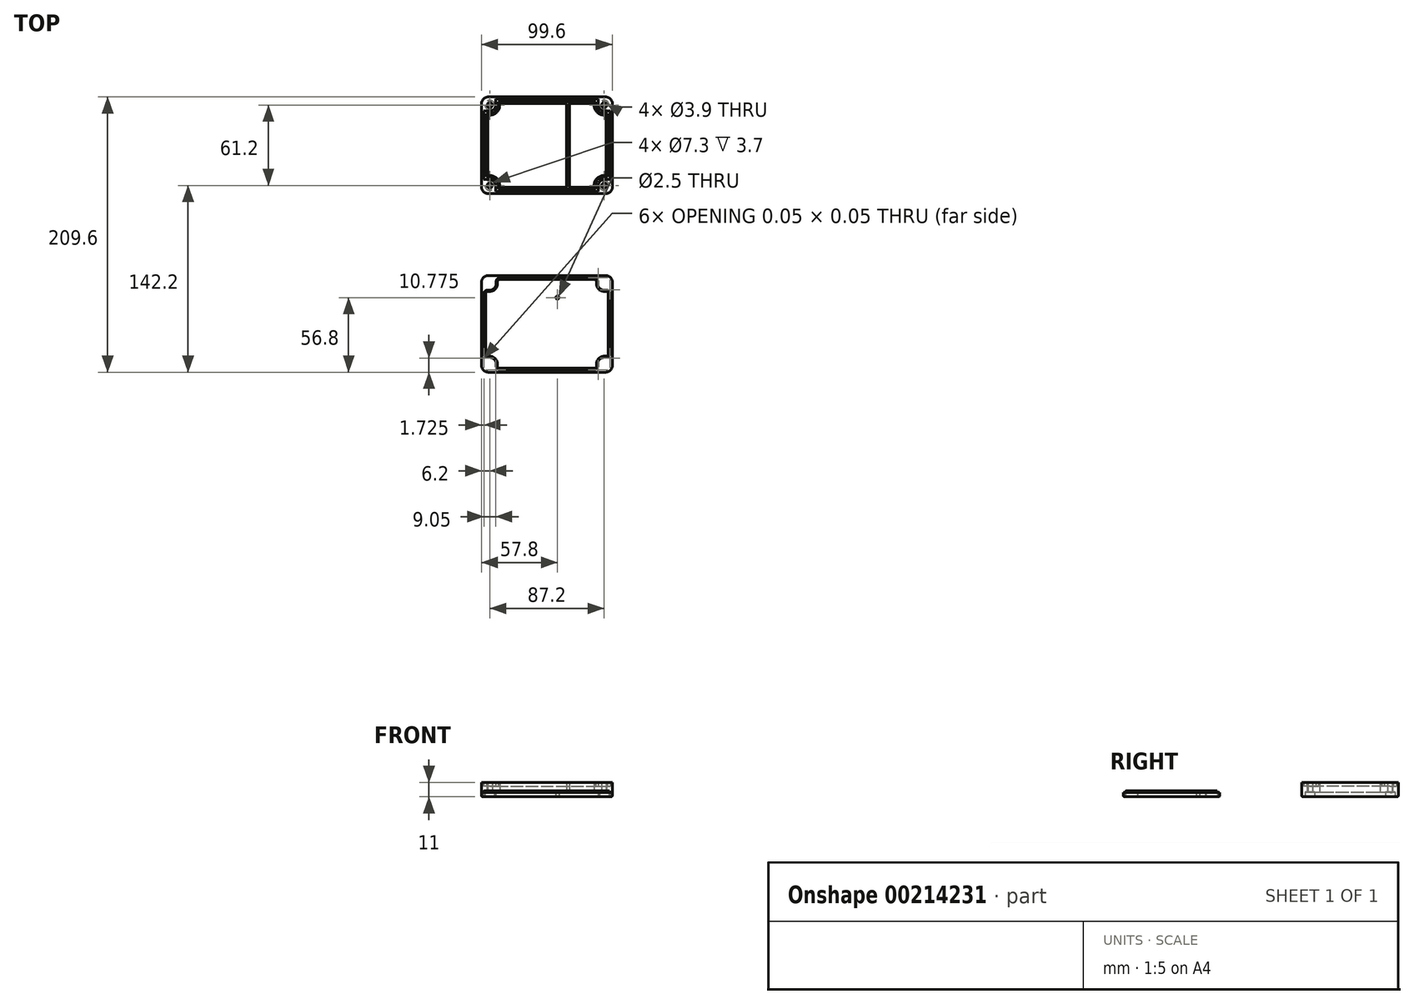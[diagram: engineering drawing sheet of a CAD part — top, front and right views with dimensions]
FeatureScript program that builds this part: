
annotation { "Feature Type Name" : "Feature", "Feature Type Description" : "" }
export const myFeature = defineFeature(function(context is Context, id is Id, definition is map)
    precondition{}
    {
        {
            var Q0;
            Q0=qCreatedBy(makeId("Top.planeOp"),FACE);
            var sketch = newSketch(context, id + "F0", { "sketchPlane" : qUnion([Q0])});
            skLineSegment(sketch, "E0.bottom", {"start": v(-25, 25) * mm, "end": v(25, 25) * mm, "construction": true});
            skLineSegment(sketch, "E0.top", {"start": v(-25, -25) * mm, "end": v(25, -25) * mm, "construction": true});
            skLineSegment(sketch, "E0.left", {"start": v(-25, 25) * mm, "end": v(-25, -25) * mm, "construction": true});
            skLineSegment(sketch, "E0.right", {"start": v(25, 25) * mm, "end": v(25, -25) * mm, "construction": true});
            skPoint(sketch, "E0.middle", {"position": v(0, 0) * mm});
            skLineSegment(sketch, "E1", {"start": v(-24, 32) * mm, "end": v(27, 32) * mm});
            skLineSegment(sketch, "E2", {"start": v(-33, 23) * mm, "end": v(-33, -23) * mm});
            skLineSegment(sketch, "E3", {"start": v(-24, -32) * mm, "end": v(27, -32) * mm});
            skLineSegment(sketch, "E4", {"start": v(28, 61.53) * mm, "end": v(28, -64.08) * mm, "construction": true});
            skLineSegment(sketch, "E5.bottom", {"start": v(31, 30) * mm, "end": v(47, 30) * mm, "construction": true});
            skLineSegment(sketch, "E5.top", {"start": v(31, -30) * mm, "end": v(47, -30) * mm, "construction": true});
            skLineSegment(sketch, "E5.left", {"start": v(31, 30) * mm, "end": v(31, -30) * mm, "construction": true});
            skLineSegment(sketch, "E5.right", {"start": v(47, 30) * mm, "end": v(47, -30) * mm, "construction": true});
            skPoint(sketch, "E5.middle", {"position": v(39, 0) * mm});
            skLineSegment(sketch, "E6", {"start": v(57, 23) * mm, "end": v(57, -23) * mm});
            skLineSegment(sketch, "E7", {"start": v(-32.8, 36.8) * mm, "end": v(56.8, 36.8) * mm});
            skLineSegment(sketch, "E8", {"start": v(-37.8, 31.8) * mm, "end": v(-37.8, -31.8) * mm});
            skLineSegment(sketch, "E9", {"start": v(-32.8, -36.8) * mm, "end": v(56.8, -36.8) * mm});
            skLineSegment(sketch, "E10", {"start": v(61.8, -31.8) * mm, "end": v(61.8, 31.8) * mm});
            skCircle(sketch, "E11", {"center": v(-31.6, 30.6) * mm, "radius": 1.95 * mm});
            skLineSegment(sketch, "E12.bottom", {"start": v(-25.1, 33.1) * mm, "end": v(49.1, 33.1) * mm});
            skLineSegment(sketch, "E12.top", {"start": v(-25.1, -33.1) * mm, "end": v(49.1, -33.1) * mm});
            skLineSegment(sketch, "E12.left", {"start": v(-34.1, 24.1) * mm, "end": v(-34.1, -24.1) * mm});
            skLineSegment(sketch, "E12.right", {"start": v(58.1, 24.1) * mm, "end": v(58.1, -24.1) * mm});
            skLineSegment(sketch, "E13.top", {"start": v(-27.1, -35.2) * mm, "end": v(51.1, -35.2) * mm});
            skLineSegment(sketch, "E13.right", {"start": v(60.2, 26.1) * mm, "end": v(60.2, -26.1) * mm});
            skLineSegment(sketch, "E14.trimOffspring", {"start": v(-27.1, 35.2) * mm, "end": v(51.1, 35.2) * mm});
            skLineSegment(sketch, "E15.trimOffspring", {"start": v(-36.2, 26.1) * mm, "end": v(-36.2, -26.1) * mm});
            skPoint(sketch, "E16.visualSharp", {"position": v(-37.8, 36.8) * mm});
            skArc(sketch, "E16.filletArc", {"start": v(-32.8, 36.8) * mm, "mid": v(-36.34, 35.34) * mm, "end": v(-37.8, 31.8) * mm});
            skLineSegment(sketch, "E17", {"start": v(27, 32) * mm, "end": v(27, -32) * mm});
            skLineSegment(sketch, "E18.MirrorCS", {"start": v(29, 32) * mm, "end": v(29, -32) * mm});
            skLineSegment(sketch, "E19.trimOffspring", {"start": v(29, 32) * mm, "end": v(48, 32) * mm});
            skLineSegment(sketch, "E20.trimOffspring", {"start": v(29, -32) * mm, "end": v(48, -32) * mm});
            skCircle(sketch, "E21", {"center": v(55.6, 30.6) * mm, "radius": 1.95 * mm});
            skArc(sketch, "E22", {"start": v(51.1, 30.6) * mm, "mid": v(52.42, 27.42) * mm, "end": v(55.6, 26.1) * mm});
            skArc(sketch, "E23", {"start": v(49.1, 30.6) * mm, "mid": v(51, 26) * mm, "end": v(55.6, 24.1) * mm});
            skArc(sketch, "E24", {"start": v(48, 30.6) * mm, "mid": v(50.23, 25.23) * mm, "end": v(55.6, 23) * mm});
            skCircle(sketch, "E25", {"center": v(55.6, -30.6) * mm, "radius": 1.95 * mm});
            skArc(sketch, "E26", {"start": v(55.6, -26.1) * mm, "mid": v(52.42, -27.42) * mm, "end": v(51.1, -30.6) * mm});
            skArc(sketch, "E27", {"start": v(55.6, -24.1) * mm, "mid": v(51, -26) * mm, "end": v(49.1, -30.6) * mm});
            skArc(sketch, "E28", {"start": v(55.6, -23) * mm, "mid": v(50.23, -25.23) * mm, "end": v(48, -30.6) * mm});
            skCircle(sketch, "E29", {"center": v(-31.6, -30.6) * mm, "radius": 1.95 * mm});
            skArc(sketch, "E30", {"start": v(-27.1, -30.6) * mm, "mid": v(-28.42, -27.42) * mm, "end": v(-31.6, -26.1) * mm});
            skArc(sketch, "E31", {"start": v(-25.1, -30.6) * mm, "mid": v(-27, -26) * mm, "end": v(-31.6, -24.1) * mm});
            skArc(sketch, "E32", {"start": v(-24, -30.6) * mm, "mid": v(-26.23, -25.23) * mm, "end": v(-31.6, -23) * mm});
            skLineSegment(sketch, "E33", {"start": v(48, 30.6) * mm, "end": v(48, 32) * mm});
            skLineSegment(sketch, "E34", {"start": v(49.1, 30.6) * mm, "end": v(49.1, 33.1) * mm});
            skLineSegment(sketch, "E35", {"start": v(51.1, 30.6) * mm, "end": v(51.1, 35.2) * mm});
            skLineSegment(sketch, "E36", {"start": v(55.6, 23) * mm, "end": v(57, 23) * mm});
            skLineSegment(sketch, "E37", {"start": v(55.6, 24.1) * mm, "end": v(58.1, 24.1) * mm});
            skLineSegment(sketch, "E38", {"start": v(55.6, 26.1) * mm, "end": v(60.2, 26.1) * mm});
            skLineSegment(sketch, "E39", {"start": v(55.6, -23) * mm, "end": v(57, -23) * mm});
            skLineSegment(sketch, "E40", {"start": v(55.6, -26.1) * mm, "end": v(60.2, -26.1) * mm});
            skLineSegment(sketch, "E41", {"start": v(48, -30.6) * mm, "end": v(48, -32) * mm});
            skLineSegment(sketch, "E42", {"start": v(49.1, -30.6) * mm, "end": v(49.1, -33.1) * mm});
            skLineSegment(sketch, "E43", {"start": v(51.1, -30.6) * mm, "end": v(51.1, -35.2) * mm});
            skLineSegment(sketch, "E44", {"start": v(55.6, -24.1) * mm, "end": v(58.1, -24.1) * mm});
            skArc(sketch, "E45", {"start": v(-31.6, 26.1) * mm, "mid": v(-28.42, 27.42) * mm, "end": v(-27.1, 30.6) * mm});
            skArc(sketch, "E46", {"start": v(-31.6, 24.1) * mm, "mid": v(-27, 26) * mm, "end": v(-25.1, 30.6) * mm});
            skArc(sketch, "E47", {"start": v(-31.6, 23) * mm, "mid": v(-26.23, 25.23) * mm, "end": v(-24, 30.6) * mm});
            skLineSegment(sketch, "E48", {"start": v(-24, 30.6) * mm, "end": v(-24, 32) * mm});
            skLineSegment(sketch, "E49", {"start": v(-25.1, 30.6) * mm, "end": v(-25.1, 33.1) * mm});
            skLineSegment(sketch, "E50", {"start": v(-27.1, 30.6) * mm, "end": v(-27.1, 35.2) * mm});
            skLineSegment(sketch, "E51", {"start": v(-31.6, 23) * mm, "end": v(-33, 23) * mm});
            skLineSegment(sketch, "E52", {"start": v(-31.6, 24.1) * mm, "end": v(-34.1, 24.1) * mm});
            skLineSegment(sketch, "E53", {"start": v(-31.6, 26.1) * mm, "end": v(-36.2, 26.1) * mm});
            skLineSegment(sketch, "E54", {"start": v(-24, -30.6) * mm, "end": v(-24, -32) * mm});
            skLineSegment(sketch, "E55", {"start": v(-25.1, -30.6) * mm, "end": v(-25.1, -33.1) * mm});
            skLineSegment(sketch, "E56", {"start": v(-27.1, -30.6) * mm, "end": v(-27.1, -35.2) * mm});
            skLineSegment(sketch, "E57", {"start": v(-31.6, -23) * mm, "end": v(-33, -23) * mm});
            skLineSegment(sketch, "E58", {"start": v(-31.6, -24.1) * mm, "end": v(-34.1, -24.1) * mm});
            skLineSegment(sketch, "E59", {"start": v(-31.6, -26.1) * mm, "end": v(-36.2, -26.1) * mm});
            skPoint(sketch, "E60.visualSharp", {"position": v(61.8, 36.8) * mm});
            skArc(sketch, "E60.filletArc", {"start": v(61.8, 31.8) * mm, "mid": v(60.34, 35.34) * mm, "end": v(56.8, 36.8) * mm});
            skPoint(sketch, "E61.visualSharp", {"position": v(61.8, -36.8) * mm});
            skArc(sketch, "E61.filletArc", {"start": v(56.8, -36.8) * mm, "mid": v(60.34, -35.34) * mm, "end": v(61.8, -31.8) * mm});
            skPoint(sketch, "E62.visualSharp", {"position": v(-37.8, -36.8) * mm});
            skArc(sketch, "E62.filletArc", {"start": v(-37.8, -31.8) * mm, "mid": v(-36.34, -35.34) * mm, "end": v(-32.8, -36.8) * mm});
            skSolve(sketch);
        }
        {
            var Q0;
            Q0=makeQuery(id+"F0.imprint","IMPRINT",FACE,{"disambiguationData":[TD([[makeQuery(id+"F0.imprint","IMPRINT",EDGE,{"derivedFrom":sQuery(id+"F0.wireOp",EDGE,"E7")}),-1.0]])]});
            var Q1;
            Q1=makeQuery(id+"F0.imprint","IMPRINT",FACE,{"disambiguationData":[TD([[makeQuery(id+"F0.imprint","IMPRINT",EDGE,{"derivedFrom":sQuery(id+"F0.wireOp",EDGE,"E1")}),1.0]])]});
            extrude(context, id + "F1", {"entities" : qUnion([Q0, Q1]), "depth" : 11 * mm});
        }
        {
            var Q0;
            Q0=makeQuery(id+"F0.imprint","IMPRINT",FACE,{"disambiguationData":[TD([[makeQuery(id+"F0.imprint","IMPRINT",EDGE,{"derivedFrom":sQuery(id+"F0.wireOp",EDGE,"E12.bottom")}),1.0]])]});
            extrude(context, id + "F2", {"entities" : qUnion([Q0]), "operationType" : NewBodyOperationType.ADD, "depth" : 8 * mm});
        }
        {
            var Q0;
            Q0=makeQuery(id+"F0.imprint","IMPRINT",FACE,{"disambiguationData":[TD([[makeQuery(id+"F0.imprint","IMPRINT",EDGE,{"derivedFrom":sQuery(id+"F0.wireOp",EDGE,"E6")}),-1.0]])]});
            var Q1;
            Q1=makeQuery(id+"F0.imprint","IMPRINT",FACE,{"disambiguationData":[TD([[makeQuery(id+"F0.imprint","IMPRINT",EDGE,{"derivedFrom":sQuery(id+"F0.wireOp",EDGE,"E1")}),-1.0]])]});
            extrude(context, id + "F3", {"entities" : qUnion([Q0, Q1]), "operationType" : NewBodyOperationType.ADD, "depth" : 3.2 * mm});
        }
        {
            var Q0;
            Q0=qCreatedBy(makeId("Top.planeOp"),FACE);
            var sketch = newSketch(context, id + "F4", { "sketchPlane" : qUnion([Q0])});
            skLineSegment(sketch, "E63", {"start": v(0, 0) * mm, "end": v(0, -187.5) * mm, "construction": true});
            skLineSegment(sketch, "E64", {"start": v(0, -136) * mm, "end": v(-72.43, -136) * mm, "construction": true});
            skLineSegment(sketch, "E65", {"start": v(0, -136) * mm, "end": v(90.36, -136) * mm, "construction": true});
            skLineSegment(sketch, "E66.bottom", {"start": v(-25, -111) * mm, "end": v(25, -111) * mm, "construction": true});
            skLineSegment(sketch, "E66.top", {"start": v(-25, -161) * mm, "end": v(25, -161) * mm, "construction": true});
            skLineSegment(sketch, "E66.left", {"start": v(-25, -111) * mm, "end": v(-25, -161) * mm, "construction": true});
            skLineSegment(sketch, "E66.right", {"start": v(25, -111) * mm, "end": v(25, -161) * mm, "construction": true});
            skPoint(sketch, "E66.middle", {"position": v(0, -136) * mm});
            skLineSegment(sketch, "E67.bottom", {"start": v(31, -106) * mm, "end": v(47, -106) * mm, "construction": true});
            skLineSegment(sketch, "E67.top", {"start": v(31, -166) * mm, "end": v(47, -166) * mm, "construction": true});
            skLineSegment(sketch, "E67.left", {"start": v(31, -106) * mm, "end": v(31, -166) * mm, "construction": true});
            skLineSegment(sketch, "E67.right", {"start": v(47, -106) * mm, "end": v(47, -166) * mm, "construction": true});
            skPoint(sketch, "E67.middle", {"position": v(39, -136) * mm});
            skLineSegment(sketch, "E68", {"start": v(28, -80.22) * mm, "end": v(28, -200.99) * mm, "construction": true});
            skLineSegment(sketch, "E69", {"start": v(-25.2, -102.8) * mm, "end": v(49.2, -102.8) * mm});
            skLineSegment(sketch, "E70", {"start": v(58.2, -111.8) * mm, "end": v(58.2, -160.2) * mm});
            skLineSegment(sketch, "E71", {"start": v(49.2, -169.2) * mm, "end": v(-25.2, -169.2) * mm});
            skLineSegment(sketch, "E72", {"start": v(-34.2, -160.2) * mm, "end": v(-34.2, -111.8) * mm});
            skLineSegment(sketch, "E73", {"start": v(-32.8, -99.2) * mm, "end": v(56.8, -99.2) * mm});
            skLineSegment(sketch, "E74", {"start": v(61.8, -104.2) * mm, "end": v(61.8, -167.8) * mm});
            skLineSegment(sketch, "E75", {"start": v(56.8, -172.8) * mm, "end": v(-32.8, -172.8) * mm});
            skLineSegment(sketch, "E76", {"start": v(-37.8, -167.8) * mm, "end": v(-37.8, -104.2) * mm});
            skLineSegment(sketch, "E77", {"start": v(-27, -100.9) * mm, "end": v(51.05, -100.9) * mm});
            skLineSegment(sketch, "E78", {"start": v(60.1, -109.95) * mm, "end": v(60.1, -162.05) * mm});
            skLineSegment(sketch, "E79", {"start": v(51.05, -171.1) * mm, "end": v(-27.05, -171.1) * mm});
            skLineSegment(sketch, "E80", {"start": v(-36.1, -162.05) * mm, "end": v(-36.1, -110) * mm});
            skCircle(sketch, "E81", {"center": v(-31.6, -105.4) * mm, "radius": 1.25 * mm});
            skCircle(sketch, "E82", {"center": v(55.6, -105.4) * mm, "radius": 1.25 * mm});
            skCircle(sketch, "E83", {"center": v(55.6, -166.6) * mm, "radius": 1.25 * mm});
            skCircle(sketch, "E84", {"center": v(-31.6, -166.6) * mm, "radius": 1.25 * mm});
            skArc(sketch, "E85", {"start": v(-31.6, -110) * mm, "mid": v(-28.35, -108.65) * mm, "end": v(-27, -105.4) * mm});
            skArc(sketch, "E86", {"start": v(-31.6, -111.8) * mm, "mid": v(-27.07, -109.93) * mm, "end": v(-25.2, -105.4) * mm});
            skLineSegment(sketch, "E87", {"start": v(-25.2, -105.4) * mm, "end": v(-25.2, -102.8) * mm});
            skLineSegment(sketch, "E88", {"start": v(-31.6, -111.8) * mm, "end": v(-34.2, -111.8) * mm});
            skLineSegment(sketch, "E89", {"start": v(-31.6, -110) * mm, "end": v(-36.1, -110) * mm});
            skLineSegment(sketch, "E90", {"start": v(-27, -105.4) * mm, "end": v(-27, -100.9) * mm});
            skArc(sketch, "E91", {"start": v(51, -105.4) * mm, "mid": v(52.35, -108.65) * mm, "end": v(55.6, -110) * mm});
            skArc(sketch, "E92", {"start": v(49.2, -105.4) * mm, "mid": v(51.07, -109.93) * mm, "end": v(55.6, -111.8) * mm});
            skArc(sketch, "E93", {"start": v(-27, -166.6) * mm, "mid": v(-28.35, -163.35) * mm, "end": v(-31.6, -162) * mm});
            skArc(sketch, "E94", {"start": v(-36.05, -162) * mm, "mid": v(-36.07, -162.02) * mm, "end": v(-36.1, -162.05) * mm});
            skArc(sketch, "E95", {"start": v(55.6, -162) * mm, "mid": v(52.35, -163.35) * mm, "end": v(51, -166.6) * mm});
            skArc(sketch, "E96", {"start": v(51, -171.05) * mm, "mid": v(51.02, -171.07) * mm, "end": v(51.05, -171.1) * mm});
            skLineSegment(sketch, "E97", {"start": v(49.2, -105.4) * mm, "end": v(49.2, -102.8) * mm});
            skLineSegment(sketch, "E98", {"start": v(51, -105.4) * mm, "end": v(51, -100.9) * mm});
            skLineSegment(sketch, "E99", {"start": v(55.6, -111.8) * mm, "end": v(58.2, -111.8) * mm});
            skLineSegment(sketch, "E100", {"start": v(55.6, -110) * mm, "end": v(60.1, -110) * mm});
            skLineSegment(sketch, "E101", {"start": v(55.6, -160.2) * mm, "end": v(58.2, -160.2) * mm});
            skLineSegment(sketch, "E102", {"start": v(55.6, -162) * mm, "end": v(60.1, -162) * mm});
            skLineSegment(sketch, "E103", {"start": v(49.2, -166.6) * mm, "end": v(49.2, -169.2) * mm});
            skLineSegment(sketch, "E104", {"start": v(51, -166.6) * mm, "end": v(51, -171.1) * mm});
            skLineSegment(sketch, "E105", {"start": v(-31.6, -160.2) * mm, "end": v(-34.2, -160.2) * mm});
            skLineSegment(sketch, "E106", {"start": v(-36.1, -162) * mm, "end": v(-31.6, -162) * mm});
            skLineSegment(sketch, "E107", {"start": v(-25.2, -166.6) * mm, "end": v(-25.2, -169.2) * mm});
            skLineSegment(sketch, "E108", {"start": v(-27, -166.6) * mm, "end": v(-27, -171.1) * mm});
            skArc(sketch, "E109.trimOffspring", {"start": v(51.05, -100.9) * mm, "mid": v(51.02, -100.93) * mm, "end": v(51, -100.95) * mm});
            skArc(sketch, "E110.trimOffspring", {"start": v(60.05, -110) * mm, "mid": v(60.07, -109.98) * mm, "end": v(60.1, -109.95) * mm});
            skArc(sketch, "E111.trimOffspring", {"start": v(60.1, -162.05) * mm, "mid": v(60.07, -162.02) * mm, "end": v(60.05, -162) * mm});
            skArc(sketch, "E112.trimOffspring", {"start": v(55.6, -160.2) * mm, "mid": v(51.07, -162.07) * mm, "end": v(49.2, -166.6) * mm});
            skArc(sketch, "E113.trimOffspring", {"start": v(-27.05, -171.1) * mm, "mid": v(-27.02, -171.07) * mm, "end": v(-27, -171.05) * mm});
            skArc(sketch, "E114.trimOffspring", {"start": v(-25.2, -166.6) * mm, "mid": v(-27.07, -162.07) * mm, "end": v(-31.6, -160.2) * mm});
            skCircle(sketch, "E115", {"center": v(-20, -116) * mm, "radius": 1.25 * mm});
            skCircle(sketch, "E116", {"center": v(-20, -116) * mm, "radius": 2.75 * mm});
            skCircle(sketch, "E117.MirrorC", {"center": v(20, -116) * mm, "radius": 2.75 * mm});
            skCircle(sketch, "E118.MirrorC", {"center": v(20, -116) * mm, "radius": 1.25 * mm});
            skCircle(sketch, "E119.MirrorC", {"center": v(-20, -156) * mm, "radius": 1.25 * mm});
            skCircle(sketch, "E120.MirrorC", {"center": v(-20, -156) * mm, "radius": 2.75 * mm});
            skCircle(sketch, "E121.MirrorC", {"center": v(20, -156) * mm, "radius": 1.25 * mm});
            skCircle(sketch, "E122.MirrorC", {"center": v(20, -156) * mm, "radius": 2.75 * mm});
            skPoint(sketch, "E123.visualSharp", {"position": v(-37.8, -99.2) * mm});
            skArc(sketch, "E123.filletArc", {"start": v(-32.8, -99.2) * mm, "mid": v(-36.34, -100.66) * mm, "end": v(-37.8, -104.2) * mm});
            skPoint(sketch, "E124.visualSharp", {"position": v(61.8, -99.2) * mm});
            skArc(sketch, "E124.filletArc", {"start": v(61.8, -104.2) * mm, "mid": v(60.34, -100.66) * mm, "end": v(56.8, -99.2) * mm});
            skPoint(sketch, "E125.visualSharp", {"position": v(61.8, -172.8) * mm});
            skArc(sketch, "E125.filletArc", {"start": v(56.8, -172.8) * mm, "mid": v(60.34, -171.34) * mm, "end": v(61.8, -167.8) * mm});
            skPoint(sketch, "E126.visualSharp", {"position": v(-37.8, -172.8) * mm});
            skArc(sketch, "E126.filletArc", {"start": v(-37.8, -167.8) * mm, "mid": v(-36.34, -171.34) * mm, "end": v(-32.8, -172.8) * mm});
            skLineSegment(sketch, "E127", {"start": v(27, -102.8) * mm, "end": v(27, -169.2) * mm});
            skLineSegment(sketch, "E128", {"start": v(29, -102.8) * mm, "end": v(29, -169.2) * mm});
            skSolve(sketch);
        }
        {
            var Q0;
            Q0=makeQuery(id+"F4.imprint","IMPRINT",FACE,{"disambiguationData":[TD([[makeQuery(id+"F4.imprint","IMPRINT",EDGE,{"derivedFrom":sQuery(id+"F4.wireOp",EDGE,"E73")}),-1.0]])]});
            var Q1;
            {var subQ0=sQuery(id+"F4.wireOp",EDGE,"E127");Q1=makeQuery(id+"F4.imprint","IMPRINT",FACE,{"disambiguationData":[TD([[makeQuery(id+"F4.imprint","IMPRINT",EDGE,{"derivedFrom":subQ0}),1.0]])]});}
            extrude(context, id + "F5", {"entities" : qUnion([Q0, Q1]), "depth" : 3.2 * mm});
        }
        {
            var Q0;
            Q0=makeQuery(id+"F4.imprint","IMPRINT",FACE,{"disambiguationData":[TD([[makeQuery(id+"F4.imprint","IMPRINT",EDGE,{"derivedFrom":sQuery(id+"F4.wireOp",EDGE,"E70")}),1.0]])]});
            extrude(context, id + "F6", {"entities" : qUnion([Q0]), "operationType" : NewBodyOperationType.ADD, "depth" : 4.7 * mm});
        }
        {
            var Q0;
            Q0=makeQuery(id+"F4.imprint","IMPRINT",FACE,{"disambiguationData":[TD([[makeQuery(id+"F4.imprint","IMPRINT",EDGE,{"derivedFrom":sQuery(id+"F4.wireOp",EDGE,"E81")}),1.0]])]});
            var Q1;
            Q1=makeQuery(id+"F4.imprint","IMPRINT",FACE,{"disambiguationData":[TD([[makeQuery(id+"F4.imprint","IMPRINT",EDGE,{"derivedFrom":sQuery(id+"F4.wireOp",EDGE,"E82")}),1.0]])]});
            var Q2;
            Q2=makeQuery(id+"F4.imprint","IMPRINT",FACE,{"disambiguationData":[TD([[makeQuery(id+"F4.imprint","IMPRINT",EDGE,{"derivedFrom":sQuery(id+"F4.wireOp",EDGE,"E84")}),1.0]])]});
            var Q3;
            Q3=makeQuery(id+"F4.imprint","IMPRINT",FACE,{"disambiguationData":[TD([[makeQuery(id+"F4.imprint","IMPRINT",EDGE,{"derivedFrom":sQuery(id+"F4.wireOp",EDGE,"E83")}),1.0]])]});
            var Q4;
            Q4=makeQuery(id+"F4.imprint","IMPRINT",FACE,{"disambiguationData":[TD([[makeQuery(id+"F4.imprint","IMPRINT",EDGE,{"derivedFrom":sQuery(id+"F4.wireOp",EDGE,"E70")}),-1.0]])]});
            var Q5;
            Q5=makeQuery(id+"F4.imprint","IMPRINT",FACE,{"disambiguationData":[TD([[makeQuery(id+"F4.imprint","IMPRINT",EDGE,{"derivedFrom":sQuery(id+"F4.wireOp",EDGE,"E72")}),-1.0]])]});
            extrude(context, id + "F7", {"entities" : qUnion([Q0, Q1, Q2, Q3, Q4, Q5]), "operationType" : NewBodyOperationType.ADD, "depth" : 3.2 * mm});
        }
        {
            var Q0;
            Q0=makeQuery(id+"F4.imprint","IMPRINT",FACE,{"disambiguationData":[TD([[makeQuery(id+"F4.imprint","IMPRINT",EDGE,{"derivedFrom":sQuery(id+"F4.wireOp",EDGE,"E115")}),-1.0]])]});
            var Q1;
            Q1=makeQuery(id+"F4.imprint","IMPRINT",FACE,{"disambiguationData":[TD([[makeQuery(id+"F4.imprint","IMPRINT",EDGE,{"derivedFrom":sQuery(id+"F4.wireOp",EDGE,"E119.MirrorC")}),1.0]])]});
            var Q2;
            Q2=makeQuery(id+"F4.imprint","IMPRINT",FACE,{"disambiguationData":[TD([[makeQuery(id+"F4.imprint","IMPRINT",EDGE,{"derivedFrom":sQuery(id+"F4.wireOp",EDGE,"E121.MirrorC")}),-1.0]])]});
            var Q3;
            Q3=makeQuery(id+"F4.imprint","IMPRINT",FACE,{"disambiguationData":[TD([[makeQuery(id+"F4.imprint","IMPRINT",EDGE,{"derivedFrom":sQuery(id+"F4.wireOp",EDGE,"E117.MirrorC")}),-1.0]])]});
            var Q4;
            {var subQ0=sQuery(id+"F4.wireOp",EDGE,"E128");var subQ1=sQuery(id+"F4.wireOp",EDGE,"E71");var subQ2=sQuery(id+"F4.wireOp",EDGE,"E69");var subQ3=sQuery(id+"F4.wireOp",EDGE,"E127");Q4=makeQuery(id+"F7.boolean.opBoolean","MERGE",FACE,{"derivedFrom":[makeQuery(id+"F5.opExtrude","CAP_FACE",FACE,{"disambiguationData":[OSD([subQ2,subQ1,subQ3,subQ0])],"isStart":false}),makeQuery(id+"F7.opExtrude","CAP_FACE",FACE,{"disambiguationData":[OSD([subQ2,subQ1,sQuery(id+"F4.wireOp",EDGE,"E72"),sQuery(id+"F4.wireOp",EDGE,"E86"),sQuery(id+"F4.wireOp",EDGE,"E87"),sQuery(id+"F4.wireOp",EDGE,"E88"),sQuery(id+"F4.wireOp",EDGE,"E105"),sQuery(id+"F4.wireOp",EDGE,"E107"),sQuery(id+"F4.wireOp",EDGE,"E114.trimOffspring"),sQuery(id+"F4.wireOp",EDGE,"E116"),sQuery(id+"F4.wireOp",EDGE,"E117.MirrorC"),sQuery(id+"F4.wireOp",EDGE,"E120.MirrorC"),sQuery(id+"F4.wireOp",EDGE,"E122.MirrorC"),subQ3])],"isStart":false}),makeQuery(id+"F7.opExtrude","CAP_FACE",FACE,{"disambiguationData":[OSD([subQ2,sQuery(id+"F4.wireOp",EDGE,"E70"),subQ1,sQuery(id+"F4.wireOp",EDGE,"E92"),sQuery(id+"F4.wireOp",EDGE,"E97"),sQuery(id+"F4.wireOp",EDGE,"E99"),sQuery(id+"F4.wireOp",EDGE,"E101"),sQuery(id+"F4.wireOp",EDGE,"E103"),sQuery(id+"F4.wireOp",EDGE,"E112.trimOffspring"),subQ0])],"isStart":false})]});}
            extrude(context, id + "F8", {"entities" : qUnion([Q0, Q1, Q2, Q3]), "operationType" : NewBodyOperationType.ADD, "endBound" : BoundingType.UP_TO_SURFACE, "endBoundEntityFace" : qUnion([Q4]), "depth" : 13.2 * mm});
        }
        {
            var Q0;
            Q0=makeQuery(id+"F4.imprint","IMPRINT",FACE,{"disambiguationData":[TD([[makeQuery(id+"F4.imprint","IMPRINT",EDGE,{"derivedFrom":sQuery(id+"F4.wireOp",EDGE,"E115")}),1.0]])]});
            var Q1;
            Q1=makeQuery(id+"F4.imprint","IMPRINT",FACE,{"disambiguationData":[TD([[makeQuery(id+"F4.imprint","IMPRINT",EDGE,{"derivedFrom":sQuery(id+"F4.wireOp",EDGE,"E118.MirrorC")}),-1.0]])]});
            var Q2;
            Q2=makeQuery(id+"F4.imprint","IMPRINT",FACE,{"disambiguationData":[TD([[makeQuery(id+"F4.imprint","IMPRINT",EDGE,{"derivedFrom":sQuery(id+"F4.wireOp",EDGE,"E121.MirrorC")}),1.0]])]});
            var Q3;
            Q3=makeQuery(id+"F4.imprint","IMPRINT",FACE,{"disambiguationData":[TD([[makeQuery(id+"F4.imprint","IMPRINT",EDGE,{"derivedFrom":sQuery(id+"F4.wireOp",EDGE,"E119.MirrorC")}),-1.0]])]});
            var Q4;
            Q4=makeQuery(id+"F7.opExtrude","CAP_FACE",FACE,{"disambiguationData":[OSD([sQuery(id+"F4.wireOp",EDGE,"E69"),sQuery(id+"F4.wireOp",EDGE,"E71"),sQuery(id+"F4.wireOp",EDGE,"E72"),sQuery(id+"F4.wireOp",EDGE,"E86"),sQuery(id+"F4.wireOp",EDGE,"E87"),sQuery(id+"F4.wireOp",EDGE,"E88"),sQuery(id+"F4.wireOp",EDGE,"E105"),sQuery(id+"F4.wireOp",EDGE,"E107"),sQuery(id+"F4.wireOp",EDGE,"E114.trimOffspring"),sQuery(id+"F4.wireOp",EDGE,"E116"),sQuery(id+"F4.wireOp",EDGE,"E117.MirrorC"),sQuery(id+"F4.wireOp",EDGE,"E120.MirrorC"),sQuery(id+"F4.wireOp",EDGE,"E122.MirrorC"),sQuery(id+"F4.wireOp",EDGE,"E127")])],"isStart":false});
            extrude(context, id + "F9", {"entities" : qUnion([Q0, Q1, Q2, Q3]), "operationType" : NewBodyOperationType.ADD, "endBound" : BoundingType.UP_TO_SURFACE, "endBoundEntityFace" : qUnion([Q4]), "depth" : 25 * mm});
        }
        {
            var Q0;
            Q0=makeQuery(id+"F5.opExtrude","SWEPT_EDGE",EDGE,{"disambiguationData":[OSD([sQuery(id+"F4.wireOp",EDGE,"E69"),sQuery(id+"F4.wireOp",EDGE,"E127")])]});
            var Q1;
            Q1=makeQuery(id+"F6.opExtrude","SWEPT_EDGE",EDGE,{"disambiguationData":[OSD([sQuery(id+"F4.wireOp",EDGE,"E69"),sQuery(id+"F4.wireOp",EDGE,"E97")])]});
            var Q2;
            Q2=makeQuery(id+"F6.opExtrude","SWEPT_EDGE",EDGE,{"disambiguationData":[OSD([sQuery(id+"F4.wireOp",EDGE,"E70"),sQuery(id+"F4.wireOp",EDGE,"E99")])]});
            var Q3;
            Q3=makeQuery(id+"F6.opExtrude","SWEPT_EDGE",EDGE,{"disambiguationData":[OSD([sQuery(id+"F4.wireOp",EDGE,"E70"),sQuery(id+"F4.wireOp",EDGE,"E101")])]});
            var Q4;
            Q4=makeQuery(id+"F6.opExtrude","SWEPT_EDGE",EDGE,{"disambiguationData":[OSD([sQuery(id+"F4.wireOp",EDGE,"E71"),sQuery(id+"F4.wireOp",EDGE,"E103")])]});
            var Q5;
            Q5=makeQuery(id+"F5.opExtrude","SWEPT_EDGE",EDGE,{"disambiguationData":[OSD([sQuery(id+"F4.wireOp",EDGE,"E71"),sQuery(id+"F4.wireOp",EDGE,"E128")])]});
            var Q6;
            Q6=makeQuery(id+"F5.opExtrude","SWEPT_EDGE",EDGE,{"disambiguationData":[OSD([sQuery(id+"F4.wireOp",EDGE,"E69"),sQuery(id+"F4.wireOp",EDGE,"E128")])]});
            var Q7;
            Q7=makeQuery(id+"F5.opExtrude","SWEPT_EDGE",EDGE,{"disambiguationData":[OSD([sQuery(id+"F4.wireOp",EDGE,"E71"),sQuery(id+"F4.wireOp",EDGE,"E127")])]});
            var Q8;
            Q8=makeQuery(id+"F6.opExtrude","SWEPT_EDGE",EDGE,{"disambiguationData":[OSD([sQuery(id+"F4.wireOp",EDGE,"E69"),sQuery(id+"F4.wireOp",EDGE,"E87")])]});
            var Q9;
            Q9=makeQuery(id+"F6.opExtrude","SWEPT_EDGE",EDGE,{"disambiguationData":[OSD([sQuery(id+"F4.wireOp",EDGE,"E72"),sQuery(id+"F4.wireOp",EDGE,"E88")])]});
            var Q10;
            Q10=makeQuery(id+"F6.opExtrude","SWEPT_EDGE",EDGE,{"disambiguationData":[OSD([sQuery(id+"F4.wireOp",EDGE,"E71"),sQuery(id+"F4.wireOp",EDGE,"E107")])]});
            var Q11;
            Q11=makeQuery(id+"F6.opExtrude","SWEPT_EDGE",EDGE,{"disambiguationData":[OSD([sQuery(id+"F4.wireOp",EDGE,"E72"),sQuery(id+"F4.wireOp",EDGE,"E105")])]});
            fillet(context, id + "F10", {"entities" : qUnion([Q0, Q1, Q2, Q3, Q4, Q5, Q6, Q7, Q8, Q9, Q10, Q11]), "radius" : 1 * mm, "tangentPropagation" : true, "allowEdgeOverflow" : false});
        }
        {
            var Q0;
            Q0=makeQuery(id+"F1.opExtrude","SWEPT_EDGE",EDGE,{"disambiguationData":[OSD([sQuery(id+"F0.wireOp",EDGE,"E2"),sQuery(id+"F0.wireOp",EDGE,"E57")])]});
            var Q1;
            Q1=makeQuery(id+"F1.opExtrude","SWEPT_EDGE",EDGE,{"disambiguationData":[OSD([sQuery(id+"F0.wireOp",EDGE,"E3"),sQuery(id+"F0.wireOp",EDGE,"E54")])]});
            var Q2;
            Q2=makeQuery(id+"F1.opExtrude","SWEPT_EDGE",EDGE,{"disambiguationData":[OSD([sQuery(id+"F0.wireOp",EDGE,"E2"),sQuery(id+"F0.wireOp",EDGE,"E51")])]});
            var Q3;
            Q3=makeQuery(id+"F1.opExtrude","SWEPT_EDGE",EDGE,{"disambiguationData":[OSD([sQuery(id+"F0.wireOp",EDGE,"E1"),sQuery(id+"F0.wireOp",EDGE,"E48")])]});
            var Q4;
            Q4=makeQuery(id+"F1.opExtrude","SWEPT_EDGE",EDGE,{"disambiguationData":[OSD([sQuery(id+"F0.wireOp",EDGE,"E3"),sQuery(id+"F0.wireOp",EDGE,"E17")])]});
            var Q5;
            Q5=makeQuery(id+"F1.opExtrude","SWEPT_EDGE",EDGE,{"disambiguationData":[OSD([sQuery(id+"F0.wireOp",EDGE,"E1"),sQuery(id+"F0.wireOp",EDGE,"E17")])]});
            var Q6;
            Q6=makeQuery(id+"F1.opExtrude","SWEPT_EDGE",EDGE,{"disambiguationData":[OSD([sQuery(id+"F0.wireOp",EDGE,"E20.trimOffspring"),sQuery(id+"F0.wireOp",EDGE,"E41")])]});
            var Q7;
            Q7=makeQuery(id+"F1.opExtrude","SWEPT_EDGE",EDGE,{"disambiguationData":[OSD([sQuery(id+"F0.wireOp",EDGE,"E6"),sQuery(id+"F0.wireOp",EDGE,"E39")])]});
            var Q8;
            Q8=makeQuery(id+"F1.opExtrude","SWEPT_EDGE",EDGE,{"disambiguationData":[OSD([sQuery(id+"F0.wireOp",EDGE,"E18.MirrorCS"),sQuery(id+"F0.wireOp",EDGE,"E20.trimOffspring")])]});
            var Q9;
            Q9=makeQuery(id+"F1.opExtrude","SWEPT_EDGE",EDGE,{"disambiguationData":[OSD([sQuery(id+"F0.wireOp",EDGE,"E6"),sQuery(id+"F0.wireOp",EDGE,"E36")])]});
            var Q10;
            Q10=makeQuery(id+"F1.opExtrude","SWEPT_EDGE",EDGE,{"disambiguationData":[OSD([sQuery(id+"F0.wireOp",EDGE,"E19.trimOffspring"),sQuery(id+"F0.wireOp",EDGE,"E33")])]});
            var Q11;
            Q11=makeQuery(id+"F1.opExtrude","SWEPT_EDGE",EDGE,{"disambiguationData":[OSD([sQuery(id+"F0.wireOp",EDGE,"E18.MirrorCS"),sQuery(id+"F0.wireOp",EDGE,"E19.trimOffspring")])]});
            fillet(context, id + "F11", {"entities" : qUnion([Q0, Q1, Q2, Q3, Q4, Q5, Q6, Q7, Q8, Q9, Q10, Q11]), "radius" : 1 * mm, "tangentPropagation" : true, "allowEdgeOverflow" : false});
        }
        {
            var Q0;
            {var subQ0=sQuery(id+"F0.wireOp",EDGE,"E41");var subQ1=sQuery(id+"F0.wireOp",EDGE,"E39");var subQ2=sQuery(id+"F0.wireOp",EDGE,"E36");var subQ3=sQuery(id+"F0.wireOp",EDGE,"E33");var subQ4=sQuery(id+"F0.wireOp",EDGE,"E28");var subQ5=sQuery(id+"F0.wireOp",EDGE,"E24");var subQ6=sQuery(id+"F0.wireOp",EDGE,"E20.trimOffspring");var subQ7=sQuery(id+"F0.wireOp",EDGE,"E19.trimOffspring");var subQ8=sQuery(id+"F0.wireOp",EDGE,"E18.MirrorCS");var subQ9=sQuery(id+"F0.wireOp",EDGE,"E6");var subQ10=sQuery(id+"F0.wireOp",EDGE,"E57");var subQ11=sQuery(id+"F0.wireOp",EDGE,"E54");var subQ12=sQuery(id+"F0.wireOp",EDGE,"E51");var subQ13=sQuery(id+"F0.wireOp",EDGE,"E48");var subQ14=sQuery(id+"F0.wireOp",EDGE,"E47");var subQ15=sQuery(id+"F0.wireOp",EDGE,"E32");var subQ16=sQuery(id+"F0.wireOp",EDGE,"E17");var subQ17=sQuery(id+"F0.wireOp",EDGE,"E3");var subQ18=sQuery(id+"F0.wireOp",EDGE,"E2");var subQ19=sQuery(id+"F0.wireOp",EDGE,"E1");var subQ20=sQuery(id+"F0.wireOp",EDGE,"E59");var subQ21=sQuery(id+"F0.wireOp",EDGE,"E58");var subQ22=sQuery(id+"F0.wireOp",EDGE,"E56");var subQ23=sQuery(id+"F0.wireOp",EDGE,"E55");var subQ24=sQuery(id+"F0.wireOp",EDGE,"E53");var subQ25=sQuery(id+"F0.wireOp",EDGE,"E52");var subQ26=sQuery(id+"F0.wireOp",EDGE,"E50");var subQ27=sQuery(id+"F0.wireOp",EDGE,"E49");var subQ28=sQuery(id+"F0.wireOp",EDGE,"E46");var subQ29=sQuery(id+"F0.wireOp",EDGE,"E45");var subQ30=sQuery(id+"F0.wireOp",EDGE,"E44");var subQ31=sQuery(id+"F0.wireOp",EDGE,"E43");var subQ32=sQuery(id+"F0.wireOp",EDGE,"E42");var subQ33=sQuery(id+"F0.wireOp",EDGE,"E40");var subQ34=sQuery(id+"F0.wireOp",EDGE,"E38");var subQ35=sQuery(id+"F0.wireOp",EDGE,"E37");var subQ36=sQuery(id+"F0.wireOp",EDGE,"E35");var subQ37=sQuery(id+"F0.wireOp",EDGE,"E34");var subQ38=sQuery(id+"F0.wireOp",EDGE,"E31");var subQ39=sQuery(id+"F0.wireOp",EDGE,"E30");var subQ40=sQuery(id+"F0.wireOp",EDGE,"E27");var subQ41=sQuery(id+"F0.wireOp",EDGE,"E26");var subQ42=sQuery(id+"F0.wireOp",EDGE,"E23");var subQ43=sQuery(id+"F0.wireOp",EDGE,"E22");var subQ44=sQuery(id+"F0.wireOp",EDGE,"E15.trimOffspring");var subQ45=sQuery(id+"F0.wireOp",EDGE,"E14.trimOffspring");var subQ46=sQuery(id+"F0.wireOp",EDGE,"E13.right");var subQ47=sQuery(id+"F0.wireOp",EDGE,"E13.top");var subQ48=sQuery(id+"F0.wireOp",EDGE,"E12.right");var subQ49=sQuery(id+"F0.wireOp",EDGE,"E12.left");var subQ50=sQuery(id+"F0.wireOp",EDGE,"E12.top");var subQ51=sQuery(id+"F0.wireOp",EDGE,"E12.bottom");Q0=makeQuery(id+"F3.boolean.opBoolean","MERGE",FACE,{"derivedFrom":[makeQuery(id+"F2.boolean.opBoolean","MERGE",FACE,{"derivedFrom":[makeQuery(id+"F1.opExtrude","CAP_FACE",FACE,{"disambiguationData":[OSD([subQ19,subQ18,subQ17,subQ9,subQ51,subQ50,subQ49,subQ48,subQ16,subQ8,subQ7,subQ6,subQ42,subQ5,subQ40,subQ4,subQ38,subQ15,subQ3,subQ37,subQ2,subQ35,subQ1,subQ0,subQ32,subQ30,subQ28,subQ14,subQ13,subQ27,subQ12,subQ25,subQ11,subQ23,subQ10,subQ21])],"isStart":true}),makeQuery(id+"F1.opExtrude","CAP_FACE",FACE,{"disambiguationData":[OSD([sQuery(id+"F0.wireOp",EDGE,"E7"),sQuery(id+"F0.wireOp",EDGE,"E8"),sQuery(id+"F0.wireOp",EDGE,"E9"),sQuery(id+"F0.wireOp",EDGE,"E10"),sQuery(id+"F0.wireOp",EDGE,"E11"),subQ47,subQ46,subQ45,subQ44,sQuery(id+"F0.wireOp",EDGE,"E16.filletArc"),sQuery(id+"F0.wireOp",EDGE,"E21"),subQ43,sQuery(id+"F0.wireOp",EDGE,"E25"),subQ41,sQuery(id+"F0.wireOp",EDGE,"E29"),subQ39,subQ36,subQ34,subQ33,subQ31,subQ29,subQ26,subQ24,subQ22,subQ20,sQuery(id+"F0.wireOp",EDGE,"E60.filletArc"),sQuery(id+"F0.wireOp",EDGE,"E61.filletArc"),sQuery(id+"F0.wireOp",EDGE,"E62.filletArc")])],"isStart":true}),makeQuery(id+"F2.opExtrude","CAP_FACE",FACE,{"disambiguationData":[OSD([subQ51,subQ50,subQ49,subQ48,subQ47,subQ46,subQ45,subQ44,subQ43,subQ42,subQ41,subQ40,subQ39,subQ38,subQ37,subQ36,subQ35,subQ34,subQ33,subQ32,subQ31,subQ30,subQ29,subQ28,subQ27,subQ26,subQ25,subQ24,subQ23,subQ22,subQ21,subQ20])],"isStart":true})]}),makeQuery(id+"F3.opExtrude","CAP_FACE",FACE,{"disambiguationData":[OSD([subQ19,subQ18,subQ17,subQ16,subQ15,subQ14,subQ13,subQ12,subQ11,subQ10])],"isStart":true}),makeQuery(id+"F3.opExtrude","CAP_FACE",FACE,{"disambiguationData":[OSD([subQ9,subQ8,subQ7,subQ6,subQ5,subQ4,subQ3,subQ2,subQ1,subQ0])],"isStart":true})]});}
            var sketch = newSketch(context, id + "F12", { "sketchPlane" : qUnion([Q0])});
            skCircle(sketch, "E129", {"center": v(55.6, -30.6) * mm, "radius": 3.65 * mm});
            skCircle(sketch, "E130", {"center": v(-31.6, -30.6) * mm, "radius": 3.65 * mm});
            skCircle(sketch, "E131", {"center": v(-31.6, 30.6) * mm, "radius": 3.65 * mm});
            skCircle(sketch, "E132", {"center": v(55.6, 30.6) * mm, "radius": 3.65 * mm});
            skSolve(sketch);
        }
        {
            var Q0;
            Q0=makeQuery(id+"F12.imprint","IMPRINT",FACE,{"disambiguationData":[TD([[makeQuery(id+"F12.imprint","IMPRINT",EDGE,{"derivedFrom":sQuery(id+"F12.wireOp",EDGE,"E129")}),1.0]])]});
            var Q1;
            Q1=makeQuery(id+"F12.imprint","IMPRINT",FACE,{"disambiguationData":[TD([[makeQuery(id+"F12.imprint","IMPRINT",EDGE,{"derivedFrom":sQuery(id+"F12.wireOp",EDGE,"E132")}),1.0]])]});
            var Q2;
            Q2=makeQuery(id+"F12.imprint","IMPRINT",FACE,{"disambiguationData":[TD([[makeQuery(id+"F12.imprint","IMPRINT",EDGE,{"derivedFrom":sQuery(id+"F12.wireOp",EDGE,"E130")}),1.0]])]});
            var Q3;
            Q3=makeQuery(id+"F12.imprint","IMPRINT",FACE,{"disambiguationData":[TD([[makeQuery(id+"F12.imprint","IMPRINT",EDGE,{"derivedFrom":sQuery(id+"F12.wireOp",EDGE,"E131")}),1.0]])]});
            extrude(context, id + "F13", {"entities" : qUnion([Q0, Q1, Q2, Q3]), "operationType" : NewBodyOperationType.REMOVE, "oppositeDirection" : true, "depth" : 3.7 * mm});
        }
        {
            var Q0;
            Q0=makeQuery(id+"F5.opExtrude","CAP_EDGE",EDGE,{"disambiguationData":[OSD([sQuery(id+"F4.wireOp",EDGE,"E74")])],"isStart":true});
            var Q1;
            Q1=makeQuery(id+"F5.opExtrude","CAP_EDGE",EDGE,{"disambiguationData":[OSD([sQuery(id+"F4.wireOp",EDGE,"E125.filletArc")])],"isStart":true});
            var Q2;
            Q2=makeQuery(id+"F5.opExtrude","CAP_EDGE",EDGE,{"disambiguationData":[OSD([sQuery(id+"F4.wireOp",EDGE,"E75")])],"isStart":true});
            var Q3;
            Q3=makeQuery(id+"F5.opExtrude","CAP_EDGE",EDGE,{"disambiguationData":[OSD([sQuery(id+"F4.wireOp",EDGE,"E126.filletArc")])],"isStart":true});
            var Q4;
            Q4=makeQuery(id+"F5.opExtrude","CAP_EDGE",EDGE,{"disambiguationData":[OSD([sQuery(id+"F4.wireOp",EDGE,"E76")])],"isStart":true});
            var Q5;
            Q5=makeQuery(id+"F5.opExtrude","CAP_EDGE",EDGE,{"disambiguationData":[OSD([sQuery(id+"F4.wireOp",EDGE,"E123.filletArc")])],"isStart":true});
            var Q6;
            Q6=makeQuery(id+"F5.opExtrude","CAP_EDGE",EDGE,{"disambiguationData":[OSD([sQuery(id+"F4.wireOp",EDGE,"E73")])],"isStart":true});
            var Q7;
            Q7=makeQuery(id+"F5.opExtrude","CAP_EDGE",EDGE,{"disambiguationData":[OSD([sQuery(id+"F4.wireOp",EDGE,"E124.filletArc")])],"isStart":true});
            fillet(context, id + "F14", {"entities" : qUnion([Q0, Q1, Q2, Q3, Q4, Q5, Q6, Q7]), "radius" : 1 * mm, "tangentPropagation" : true, "allowEdgeOverflow" : false});
        }
        {
            var Q0;
            Q0=makeQuery(id+"F1.opExtrude","CAP_EDGE",EDGE,{"disambiguationData":[OSD([sQuery(id+"F0.wireOp",EDGE,"E61.filletArc")])],"isStart":true});
            fillet(context, id + "F15", {"entities" : qUnion([Q0]), "radius" : 1 * mm, "tangentPropagation" : true, "allowEdgeOverflow" : false});
        }
        {
            var Q0;
            Q0=makeQuery(id+"F6.opExtrude","CAP_FACE",FACE,{"disambiguationData":[OSD([sQuery(id+"F4.wireOp",EDGE,"E69"),sQuery(id+"F4.wireOp",EDGE,"E70"),sQuery(id+"F4.wireOp",EDGE,"E71"),sQuery(id+"F4.wireOp",EDGE,"E72"),sQuery(id+"F4.wireOp",EDGE,"E77"),sQuery(id+"F4.wireOp",EDGE,"E78"),sQuery(id+"F4.wireOp",EDGE,"E79"),sQuery(id+"F4.wireOp",EDGE,"E80"),sQuery(id+"F4.wireOp",EDGE,"E85"),sQuery(id+"F4.wireOp",EDGE,"E86"),sQuery(id+"F4.wireOp",EDGE,"E87"),sQuery(id+"F4.wireOp",EDGE,"E88"),sQuery(id+"F4.wireOp",EDGE,"E89"),sQuery(id+"F4.wireOp",EDGE,"E90"),sQuery(id+"F4.wireOp",EDGE,"E91"),sQuery(id+"F4.wireOp",EDGE,"E92"),sQuery(id+"F4.wireOp",EDGE,"E93"),sQuery(id+"F4.wireOp",EDGE,"E95"),sQuery(id+"F4.wireOp",EDGE,"E97"),sQuery(id+"F4.wireOp",EDGE,"E98"),sQuery(id+"F4.wireOp",EDGE,"E99"),sQuery(id+"F4.wireOp",EDGE,"E100"),sQuery(id+"F4.wireOp",EDGE,"E101"),sQuery(id+"F4.wireOp",EDGE,"E102"),sQuery(id+"F4.wireOp",EDGE,"E103"),sQuery(id+"F4.wireOp",EDGE,"E104"),sQuery(id+"F4.wireOp",EDGE,"E105"),sQuery(id+"F4.wireOp",EDGE,"E106"),sQuery(id+"F4.wireOp",EDGE,"E107"),sQuery(id+"F4.wireOp",EDGE,"E108"),sQuery(id+"F4.wireOp",EDGE,"E112.trimOffspring"),sQuery(id+"F4.wireOp",EDGE,"E114.trimOffspring")])],"isStart":false});
            var sketch = newSketch(context, id + "F16", { "sketchPlane" : qUnion([Q0])});
            skLineSegment(sketch, "E133.0", {"start": v(-36.1, -162) * mm, "end": v(-36.1, -110) * mm});
            skLineSegment(sketch, "E133.1", {"start": v(-31.6, -110) * mm, "end": v(-36.1, -110) * mm});
            skArc(sketch, "E133.2", {"start": v(-31.6, -110) * mm, "mid": v(-28.35, -108.65) * mm, "end": v(-27, -105.4) * mm});
            skLineSegment(sketch, "E133.3", {"start": v(-27, -105.4) * mm, "end": v(-27, -100.9) * mm});
            skLineSegment(sketch, "E133.4", {"start": v(-27, -100.9) * mm, "end": v(51, -100.9) * mm});
            skLineSegment(sketch, "E133.5", {"start": v(51, -105.4) * mm, "end": v(51, -100.9) * mm});
            skArc(sketch, "E133.6", {"start": v(51, -105.4) * mm, "mid": v(52.35, -108.65) * mm, "end": v(55.6, -110) * mm});
            skLineSegment(sketch, "E133.7", {"start": v(55.6, -110) * mm, "end": v(60.1, -110) * mm});
            skLineSegment(sketch, "E133.8", {"start": v(60.1, -110) * mm, "end": v(60.1, -162) * mm});
            skLineSegment(sketch, "E133.9", {"start": v(55.6, -162) * mm, "end": v(60.1, -162) * mm});
            skArc(sketch, "E133.10", {"start": v(55.6, -162) * mm, "mid": v(52.35, -163.35) * mm, "end": v(51, -166.6) * mm});
            skLineSegment(sketch, "E133.11", {"start": v(51, -166.6) * mm, "end": v(51, -171.1) * mm});
            skLineSegment(sketch, "E133.12", {"start": v(51, -171.1) * mm, "end": v(-27, -171.1) * mm});
            skArc(sketch, "E133.13", {"start": v(-27, -166.6) * mm, "mid": v(-28.35, -163.35) * mm, "end": v(-31.6, -162) * mm});
            skLineSegment(sketch, "E133.14", {"start": v(-36.1, -162) * mm, "end": v(-31.6, -162) * mm});
            skLineSegment(sketch, "E133.15", {"start": v(-27, -166.6) * mm, "end": v(-27, -171.1) * mm});
            skLineSegment(sketch, "E134.0", {"start": v(-26.6, -105.4) * mm, "end": v(-26.6, -101.3) * mm});
            skArc(sketch, "E134.1", {"start": v(-31.6, -110.4) * mm, "mid": v(-28.06, -108.94) * mm, "end": v(-26.6, -105.4) * mm});
            skLineSegment(sketch, "E134.2", {"start": v(-31.6, -110.4) * mm, "end": v(-35.7, -110.4) * mm});
            skLineSegment(sketch, "E134.3", {"start": v(-35.7, -161.6) * mm, "end": v(-35.7, -110.4) * mm});
            skLineSegment(sketch, "E134.4", {"start": v(-35.7, -161.6) * mm, "end": v(-31.6, -161.6) * mm});
            skLineSegment(sketch, "E134.5", {"start": v(59.7, -110.4) * mm, "end": v(59.7, -161.6) * mm});
            skLineSegment(sketch, "E134.6", {"start": v(55.6, -110.4) * mm, "end": v(59.7, -110.4) * mm});
            skArc(sketch, "E134.7", {"start": v(50.6, -105.4) * mm, "mid": v(52.06, -108.94) * mm, "end": v(55.6, -110.4) * mm});
            skLineSegment(sketch, "E134.8", {"start": v(50.6, -105.4) * mm, "end": v(50.6, -101.3) * mm});
            skLineSegment(sketch, "E134.9", {"start": v(55.6, -161.6) * mm, "end": v(59.7, -161.6) * mm});
            skArc(sketch, "E134.10", {"start": v(55.6, -161.6) * mm, "mid": v(52.06, -163.06) * mm, "end": v(50.6, -166.6) * mm});
            skLineSegment(sketch, "E134.11", {"start": v(50.6, -166.6) * mm, "end": v(50.6, -170.7) * mm});
            skLineSegment(sketch, "E134.12", {"start": v(50.6, -170.7) * mm, "end": v(-26.6, -170.7) * mm});
            skLineSegment(sketch, "E134.13", {"start": v(-26.6, -166.6) * mm, "end": v(-26.6, -170.7) * mm});
            skLineSegment(sketch, "E134.14", {"start": v(-26.6, -101.3) * mm, "end": v(50.6, -101.3) * mm});
            skArc(sketch, "E134.15", {"start": v(-26.6, -166.6) * mm, "mid": v(-28.06, -163.06) * mm, "end": v(-31.6, -161.6) * mm});
            skLineSegment(sketch, "E135.0", {"start": v(-24.2, -102.8) * mm, "end": v(48.2, -102.8) * mm});
            skArc(sketch, "E135.1", {"start": v(-31.6, -111.8) * mm, "mid": v(-27.07, -109.93) * mm, "end": v(-25.2, -105.4) * mm});
            skLineSegment(sketch, "E135.2", {"start": v(-25.2, -105.4) * mm, "end": v(-25.2, -103.8) * mm});
            skArc(sketch, "E135.3", {"start": v(-25.2, -103.8) * mm, "mid": v(-24.9, -103.1) * mm, "end": v(-24.2, -102.8) * mm});
            skLineSegment(sketch, "E135.4", {"start": v(-31.6, -111.8) * mm, "end": v(-33.2, -111.8) * mm});
            skArc(sketch, "E135.5", {"start": v(-34.2, -112.8) * mm, "mid": v(-33.9, -112.1) * mm, "end": v(-33.2, -111.8) * mm});
            skLineSegment(sketch, "E135.6", {"start": v(-34.2, -159.2) * mm, "end": v(-34.2, -112.8) * mm});
            skArc(sketch, "E135.7", {"start": v(48.2, -102.8) * mm, "mid": v(48.9, -103.1) * mm, "end": v(49.2, -103.8) * mm});
            skLineSegment(sketch, "E135.8", {"start": v(49.2, -105.4) * mm, "end": v(49.2, -103.8) * mm});
            skArc(sketch, "E135.9", {"start": v(49.2, -105.4) * mm, "mid": v(51.07, -109.93) * mm, "end": v(55.6, -111.8) * mm});
            skLineSegment(sketch, "E135.10", {"start": v(55.6, -111.8) * mm, "end": v(57.2, -111.8) * mm});
            skArc(sketch, "E135.11", {"start": v(57.2, -111.8) * mm, "mid": v(57.9, -112.1) * mm, "end": v(58.2, -112.8) * mm});
            skArc(sketch, "E135.12", {"start": v(58.2, -159.2) * mm, "mid": v(57.9, -159.9) * mm, "end": v(57.2, -160.2) * mm});
            skLineSegment(sketch, "E135.13", {"start": v(55.6, -160.2) * mm, "end": v(57.2, -160.2) * mm});
            skArc(sketch, "E135.14", {"start": v(55.6, -160.2) * mm, "mid": v(51.07, -162.07) * mm, "end": v(49.2, -166.6) * mm});
            skArc(sketch, "E135.15", {"start": v(49.2, -168.2) * mm, "mid": v(48.9, -168.9) * mm, "end": v(48.2, -169.2) * mm});
            skLineSegment(sketch, "E135.16", {"start": v(49.2, -166.6) * mm, "end": v(49.2, -168.2) * mm});
            skArc(sketch, "E135.17", {"start": v(-33.2, -160.2) * mm, "mid": v(-33.9, -159.9) * mm, "end": v(-34.2, -159.2) * mm});
            skLineSegment(sketch, "E135.18", {"start": v(-31.6, -160.2) * mm, "end": v(-33.2, -160.2) * mm});
            skArc(sketch, "E135.19", {"start": v(-25.2, -166.6) * mm, "mid": v(-27.07, -162.07) * mm, "end": v(-31.6, -160.2) * mm});
            skLineSegment(sketch, "E135.20", {"start": v(-25.2, -166.6) * mm, "end": v(-25.2, -168.2) * mm});
            skArc(sketch, "E135.21", {"start": v(-24.2, -169.2) * mm, "mid": v(-24.9, -168.9) * mm, "end": v(-25.2, -168.2) * mm});
            skLineSegment(sketch, "E135.22", {"start": v(48.2, -169.2) * mm, "end": v(-24.2, -169.2) * mm});
            skLineSegment(sketch, "E135.23", {"start": v(58.2, -112.8) * mm, "end": v(58.2, -159.2) * mm});
            skArc(sketch, "E136.0", {"start": v(57.2, -111.3) * mm, "mid": v(58.26, -111.74) * mm, "end": v(58.7, -112.8) * mm});
            skLineSegment(sketch, "E136.1", {"start": v(-31.6, -160.7) * mm, "end": v(-33.2, -160.7) * mm});
            skArc(sketch, "E136.2", {"start": v(-25.7, -166.6) * mm, "mid": v(-27.43, -162.43) * mm, "end": v(-31.6, -160.7) * mm});
            skLineSegment(sketch, "E136.3", {"start": v(-25.7, -166.6) * mm, "end": v(-25.7, -168.2) * mm});
            skArc(sketch, "E136.4", {"start": v(-24.2, -169.7) * mm, "mid": v(-25.26, -169.26) * mm, "end": v(-25.7, -168.2) * mm});
            skLineSegment(sketch, "E136.5", {"start": v(48.2, -169.7) * mm, "end": v(-24.2, -169.7) * mm});
            skArc(sketch, "E136.6", {"start": v(49.7, -168.2) * mm, "mid": v(49.26, -169.26) * mm, "end": v(48.2, -169.7) * mm});
            skArc(sketch, "E136.7", {"start": v(58.7, -159.2) * mm, "mid": v(58.26, -160.26) * mm, "end": v(57.2, -160.7) * mm});
            skLineSegment(sketch, "E136.8", {"start": v(55.6, -160.7) * mm, "end": v(57.2, -160.7) * mm});
            skArc(sketch, "E136.9", {"start": v(55.6, -160.7) * mm, "mid": v(51.43, -162.43) * mm, "end": v(49.7, -166.6) * mm});
            skLineSegment(sketch, "E136.10", {"start": v(49.7, -166.6) * mm, "end": v(49.7, -168.2) * mm});
            skArc(sketch, "E136.11", {"start": v(-33.2, -160.7) * mm, "mid": v(-34.26, -160.26) * mm, "end": v(-34.7, -159.2) * mm});
            skLineSegment(sketch, "E136.12", {"start": v(58.7, -112.8) * mm, "end": v(58.7, -159.2) * mm});
            skLineSegment(sketch, "E136.13", {"start": v(-34.7, -159.2) * mm, "end": v(-34.7, -112.8) * mm});
            skArc(sketch, "E136.14", {"start": v(-34.7, -112.8) * mm, "mid": v(-34.26, -111.74) * mm, "end": v(-33.2, -111.3) * mm});
            skLineSegment(sketch, "E136.15", {"start": v(-31.6, -111.3) * mm, "end": v(-33.2, -111.3) * mm});
            skArc(sketch, "E136.16", {"start": v(-31.6, -111.3) * mm, "mid": v(-27.43, -109.57) * mm, "end": v(-25.7, -105.4) * mm});
            skLineSegment(sketch, "E136.17", {"start": v(-25.7, -105.4) * mm, "end": v(-25.7, -103.8) * mm});
            skArc(sketch, "E136.18", {"start": v(-25.7, -103.8) * mm, "mid": v(-25.26, -102.74) * mm, "end": v(-24.2, -102.3) * mm});
            skLineSegment(sketch, "E136.19", {"start": v(-24.2, -102.3) * mm, "end": v(48.2, -102.3) * mm});
            skArc(sketch, "E136.20", {"start": v(48.2, -102.3) * mm, "mid": v(49.26, -102.74) * mm, "end": v(49.7, -103.8) * mm});
            skLineSegment(sketch, "E136.21", {"start": v(49.7, -105.4) * mm, "end": v(49.7, -103.8) * mm});
            skArc(sketch, "E136.22", {"start": v(49.7, -105.4) * mm, "mid": v(51.43, -109.57) * mm, "end": v(55.6, -111.3) * mm});
            skLineSegment(sketch, "E136.23", {"start": v(55.6, -111.3) * mm, "end": v(57.2, -111.3) * mm});
            skSolve(sketch);
        }
        {
            var Q0;
            Q0=makeQuery(id+"F16.imprint","IMPRINT",FACE,{"disambiguationData":[TD([[makeQuery(id+"F16.imprint","IMPRINT",EDGE,{"derivedFrom":sQuery(id+"F16.wireOp",EDGE,"E133.0")}),-1.0]])]});
            var Q1;
            Q1=makeQuery(id+"F5.opExtrude","CAP_FACE",FACE,{"disambiguationData":[OSD([sQuery(id+"F4.wireOp",EDGE,"E73"),sQuery(id+"F4.wireOp",EDGE,"E74"),sQuery(id+"F4.wireOp",EDGE,"E75"),sQuery(id+"F4.wireOp",EDGE,"E76"),sQuery(id+"F4.wireOp",EDGE,"E77"),sQuery(id+"F4.wireOp",EDGE,"E78"),sQuery(id+"F4.wireOp",EDGE,"E79"),sQuery(id+"F4.wireOp",EDGE,"E80"),sQuery(id+"F4.wireOp",EDGE,"E81"),sQuery(id+"F4.wireOp",EDGE,"E82"),sQuery(id+"F4.wireOp",EDGE,"E83"),sQuery(id+"F4.wireOp",EDGE,"E84"),sQuery(id+"F4.wireOp",EDGE,"E85"),sQuery(id+"F4.wireOp",EDGE,"E89"),sQuery(id+"F4.wireOp",EDGE,"E90"),sQuery(id+"F4.wireOp",EDGE,"E91"),sQuery(id+"F4.wireOp",EDGE,"E93"),sQuery(id+"F4.wireOp",EDGE,"E94"),sQuery(id+"F4.wireOp",EDGE,"E95"),sQuery(id+"F4.wireOp",EDGE,"E96"),sQuery(id+"F4.wireOp",EDGE,"E98"),sQuery(id+"F4.wireOp",EDGE,"E100"),sQuery(id+"F4.wireOp",EDGE,"E102"),sQuery(id+"F4.wireOp",EDGE,"E104"),sQuery(id+"F4.wireOp",EDGE,"E106"),sQuery(id+"F4.wireOp",EDGE,"E108"),sQuery(id+"F4.wireOp",EDGE,"E109.trimOffspring"),sQuery(id+"F4.wireOp",EDGE,"E110.trimOffspring"),sQuery(id+"F4.wireOp",EDGE,"E111.trimOffspring"),sQuery(id+"F4.wireOp",EDGE,"E113.trimOffspring"),sQuery(id+"F4.wireOp",EDGE,"E123.filletArc"),sQuery(id+"F4.wireOp",EDGE,"E124.filletArc"),sQuery(id+"F4.wireOp",EDGE,"E125.filletArc"),sQuery(id+"F4.wireOp",EDGE,"E126.filletArc")])],"isStart":false});
            extrude(context, id + "F17", {"entities" : qUnion([Q0]), "operationType" : NewBodyOperationType.REMOVE, "endBound" : BoundingType.UP_TO_SURFACE, "oppositeDirection" : true, "endBoundEntityFace" : qUnion([Q1]), "depth" : 25 * mm});
        }
        {
            var Q0;
            Q0=makeQuery(id+"F16.imprint","IMPRINT",FACE,{"disambiguationData":[TD([[makeQuery(id+"F16.imprint","IMPRINT",EDGE,{"derivedFrom":sQuery(id+"F16.wireOp",EDGE,"E135.0")}),1.0]])]});
            var Q1;
            {var subQ0=sQuery(id+"F4.wireOp",EDGE,"E126.filletArc");var subQ1=sQuery(id+"F4.wireOp",EDGE,"E125.filletArc");var subQ2=sQuery(id+"F4.wireOp",EDGE,"E124.filletArc");var subQ3=sQuery(id+"F4.wireOp",EDGE,"E123.filletArc");var subQ4=sQuery(id+"F4.wireOp",EDGE,"E113.trimOffspring");var subQ5=sQuery(id+"F4.wireOp",EDGE,"E111.trimOffspring");var subQ6=sQuery(id+"F4.wireOp",EDGE,"E110.trimOffspring");var subQ7=sQuery(id+"F4.wireOp",EDGE,"E109.trimOffspring");var subQ8=sQuery(id+"F4.wireOp",EDGE,"E108");var subQ9=sQuery(id+"F4.wireOp",EDGE,"E106");var subQ10=sQuery(id+"F4.wireOp",EDGE,"E104");var subQ11=sQuery(id+"F4.wireOp",EDGE,"E102");var subQ12=sQuery(id+"F4.wireOp",EDGE,"E100");var subQ13=sQuery(id+"F4.wireOp",EDGE,"E98");var subQ14=sQuery(id+"F4.wireOp",EDGE,"E96");var subQ15=sQuery(id+"F4.wireOp",EDGE,"E95");var subQ16=sQuery(id+"F4.wireOp",EDGE,"E94");var subQ17=sQuery(id+"F4.wireOp",EDGE,"E93");var subQ18=sQuery(id+"F4.wireOp",EDGE,"E91");var subQ19=sQuery(id+"F4.wireOp",EDGE,"E90");var subQ20=sQuery(id+"F4.wireOp",EDGE,"E89");var subQ21=sQuery(id+"F4.wireOp",EDGE,"E85");var subQ22=sQuery(id+"F4.wireOp",EDGE,"E84");var subQ23=sQuery(id+"F4.wireOp",EDGE,"E83");var subQ24=sQuery(id+"F4.wireOp",EDGE,"E82");var subQ25=sQuery(id+"F4.wireOp",EDGE,"E81");var subQ26=sQuery(id+"F4.wireOp",EDGE,"E80");var subQ27=sQuery(id+"F4.wireOp",EDGE,"E79");var subQ28=sQuery(id+"F4.wireOp",EDGE,"E78");var subQ29=sQuery(id+"F4.wireOp",EDGE,"E77");var subQ30=sQuery(id+"F4.wireOp",EDGE,"E76");var subQ31=sQuery(id+"F4.wireOp",EDGE,"E75");var subQ32=sQuery(id+"F4.wireOp",EDGE,"E74");var subQ33=sQuery(id+"F4.wireOp",EDGE,"E73");Q1=makeQuery(id+"F17.boolean.opBoolean","MERGE",FACE,{"derivedFrom":[makeQuery(id+"F5.opExtrude","CAP_FACE",FACE,{"disambiguationData":[OSD([subQ33,subQ32,subQ31,subQ30,subQ29,subQ28,subQ27,subQ26,subQ25,subQ24,subQ23,subQ22,subQ21,subQ20,subQ19,subQ18,subQ17,subQ16,subQ15,subQ14,subQ13,subQ12,subQ11,subQ10,subQ9,subQ8,subQ7,subQ6,subQ5,subQ4,subQ3,subQ2,subQ1,subQ0])],"isStart":false}),makeQuery(id+"F17.opExtrude","CAP_FACE",FACE,{"disambiguationData":[OSD([subQ33,subQ32,subQ31,subQ30,subQ29,subQ28,subQ27,subQ26,subQ25,subQ24,subQ23,subQ22,subQ21,subQ20,subQ19,subQ18,subQ17,subQ16,subQ15,subQ14,subQ13,subQ12,subQ11,subQ10,subQ9,subQ8,subQ7,subQ6,subQ5,subQ4,subQ3,subQ2,subQ1,subQ0])],"isStart":false})]});}
            extrude(context, id + "F18", {"entities" : qUnion([Q0]), "operationType" : NewBodyOperationType.REMOVE, "endBound" : BoundingType.UP_TO_SURFACE, "oppositeDirection" : true, "endBoundEntityFace" : qUnion([Q1]), "depth" : 25 * mm});
        }
        {
            var Q0;
            Q0=makeQuery(id+"F17.boolean.opBoolean","COPY",EDGE,{"derivedFrom":makeQuery(id+"F17.opExtrude","SWEPT_EDGE",EDGE,{"disambiguationData":[OSD([sQuery(id+"F16.wireOp",EDGE,"E134.5"),sQuery(id+"F16.wireOp",EDGE,"E134.9")])]})});
            var Q1;
            Q1=makeQuery(id+"F17.boolean.opBoolean","COPY",EDGE,{"derivedFrom":makeQuery(id+"F17.opExtrude","SWEPT_EDGE",EDGE,{"disambiguationData":[OSD([sQuery(id+"F16.wireOp",EDGE,"E134.11"),sQuery(id+"F16.wireOp",EDGE,"E134.12")])]})});
            var Q2;
            Q2=makeQuery(id+"F17.boolean.opBoolean","COPY",EDGE,{"derivedFrom":makeQuery(id+"F17.opExtrude","SWEPT_EDGE",EDGE,{"disambiguationData":[OSD([sQuery(id+"F16.wireOp",EDGE,"E134.12"),sQuery(id+"F16.wireOp",EDGE,"E134.13")])]})});
            var Q3;
            Q3=makeQuery(id+"F17.boolean.opBoolean","COPY",EDGE,{"derivedFrom":makeQuery(id+"F17.opExtrude","SWEPT_EDGE",EDGE,{"disambiguationData":[OSD([sQuery(id+"F16.wireOp",EDGE,"E134.3"),sQuery(id+"F16.wireOp",EDGE,"E134.4")])]})});
            var Q4;
            Q4=makeQuery(id+"F17.boolean.opBoolean","COPY",EDGE,{"derivedFrom":makeQuery(id+"F17.opExtrude","SWEPT_EDGE",EDGE,{"disambiguationData":[OSD([sQuery(id+"F16.wireOp",EDGE,"E134.2"),sQuery(id+"F16.wireOp",EDGE,"E134.3")])]})});
            var Q5;
            Q5=makeQuery(id+"F17.boolean.opBoolean","COPY",EDGE,{"derivedFrom":makeQuery(id+"F17.opExtrude","SWEPT_EDGE",EDGE,{"disambiguationData":[OSD([sQuery(id+"F16.wireOp",EDGE,"E134.0"),sQuery(id+"F16.wireOp",EDGE,"E134.14")])]})});
            var Q6;
            Q6=makeQuery(id+"F17.boolean.opBoolean","COPY",EDGE,{"derivedFrom":makeQuery(id+"F17.opExtrude","SWEPT_EDGE",EDGE,{"disambiguationData":[OSD([sQuery(id+"F16.wireOp",EDGE,"E134.8"),sQuery(id+"F16.wireOp",EDGE,"E134.14")])]})});
            var Q7;
            Q7=makeQuery(id+"F17.boolean.opBoolean","COPY",EDGE,{"derivedFrom":makeQuery(id+"F17.opExtrude","SWEPT_EDGE",EDGE,{"disambiguationData":[OSD([sQuery(id+"F16.wireOp",EDGE,"E134.5"),sQuery(id+"F16.wireOp",EDGE,"E134.6")])]})});
            fillet(context, id + "F19", {"entities" : qUnion([Q0, Q1, Q2, Q3, Q4, Q5, Q6, Q7]), "radius" : 2 * mm, "tangentPropagation" : true, "allowEdgeOverflow" : false});
        }
    });
